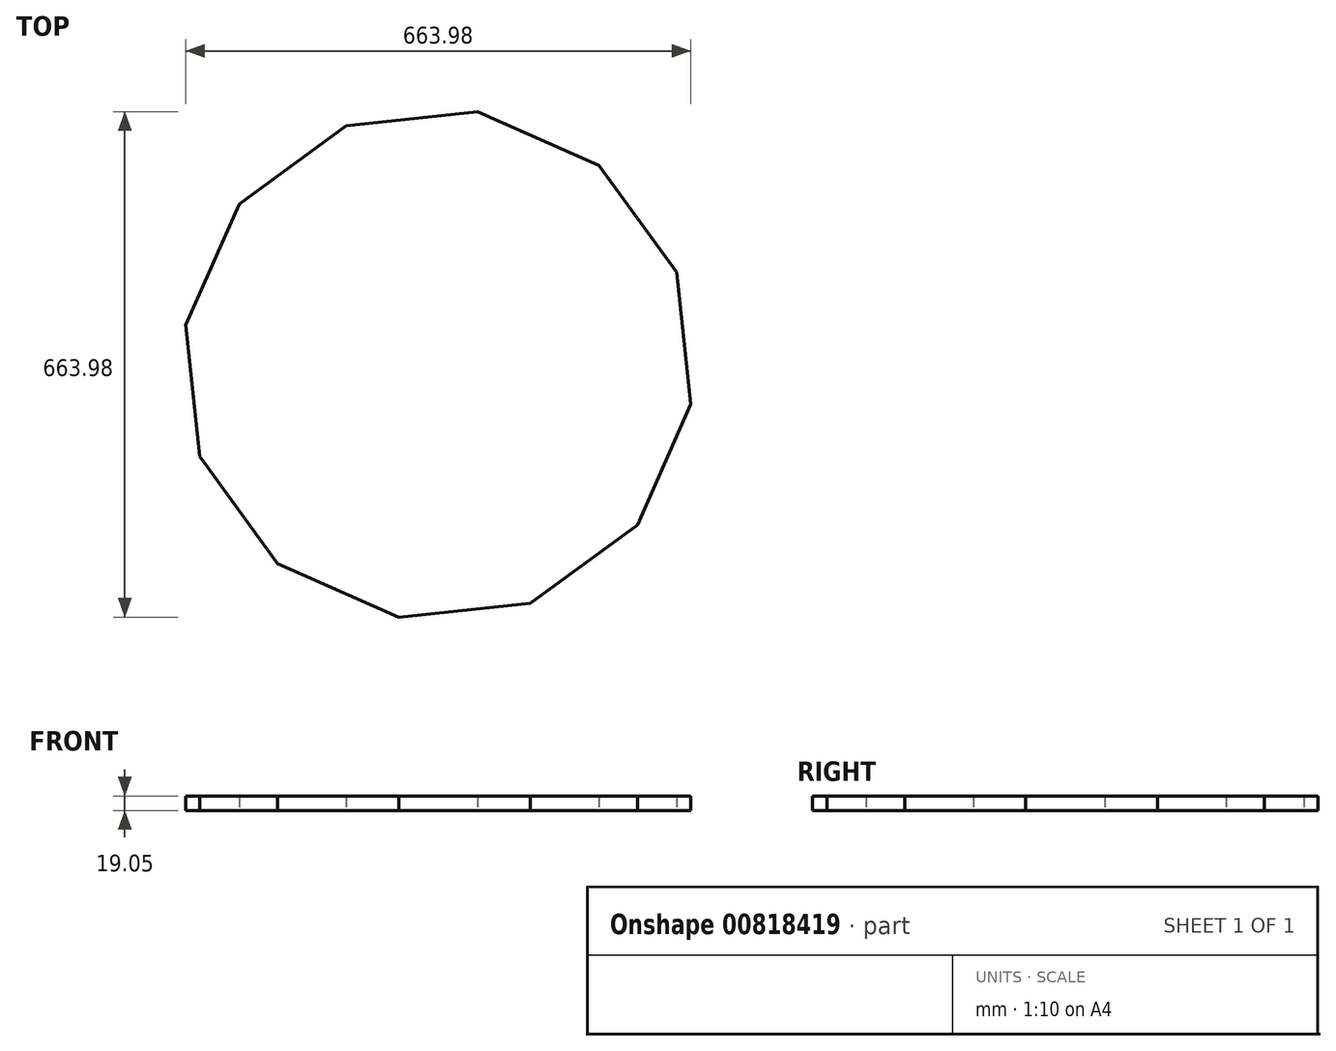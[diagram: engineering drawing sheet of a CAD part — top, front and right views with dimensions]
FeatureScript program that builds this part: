
annotation { "Feature Type Name" : "Feature", "Feature Type Description" : "" }
export const myFeature = defineFeature(function(context is Context, id is Id, definition is map)
    precondition{}
    {
        {
            var Q0;
            Q0=qCreatedBy(makeId("Top.planeOp"),FACE);
            var sketch = newSketch(context, id + "F0", { "sketchPlane" : qUnion([Q0])});
            skCircle(sketch, "E0.cCircle", {"center": v(0, 0) * mm, "radius": 336.03 * mm, "construction": true});
            skLineSegment(sketch, "E0.0", {"start": v(261.53, -210.98) * mm, "end": v(121, -313.49) * mm});
            skLineSegment(sketch, "E0.1", {"start": v(121, -313.49) * mm, "end": v(-51.95, -331.99) * mm});
            skLineSegment(sketch, "E0.2", {"start": v(-51.95, -331.99) * mm, "end": v(-210.98, -261.53) * mm});
            skLineSegment(sketch, "E0.3", {"start": v(-210.98, -261.53) * mm, "end": v(-313.49, -121) * mm});
            skLineSegment(sketch, "E0.4", {"start": v(-313.49, -121) * mm, "end": v(-331.99, 51.95) * mm});
            skLineSegment(sketch, "E0.5", {"start": v(-331.99, 51.95) * mm, "end": v(-261.53, 210.98) * mm});
            skLineSegment(sketch, "E0.6", {"start": v(-261.53, 210.98) * mm, "end": v(-121, 313.49) * mm});
            skLineSegment(sketch, "E0.7", {"start": v(-121, 313.49) * mm, "end": v(51.95, 331.99) * mm});
            skLineSegment(sketch, "E0.8", {"start": v(51.95, 331.99) * mm, "end": v(210.98, 261.53) * mm});
            skLineSegment(sketch, "E0.9", {"start": v(210.98, 261.53) * mm, "end": v(313.49, 121) * mm});
            skLineSegment(sketch, "E0.10", {"start": v(313.49, 121) * mm, "end": v(331.99, -51.95) * mm});
            skLineSegment(sketch, "E0.11", {"start": v(331.99, -51.95) * mm, "end": v(261.53, -210.98) * mm});
            skSolve(sketch);
        }
        {
            var Q0;
            Q0=makeQuery(id+"F0.imprint","IMPRINT",FACE,{"disambiguationData":[TD([[makeQuery(id+"F0.imprint","IMPRINT",EDGE,{"derivedFrom":sQuery(id+"F0.wireOp",EDGE,"E0.0")}),-1.0]])]});
            extrude(context, id + "F1", {"entities" : qUnion([Q0]), "depth" : 19.05 * mm, "offsetDistance" : 25.4 * mm});
        }
    });
